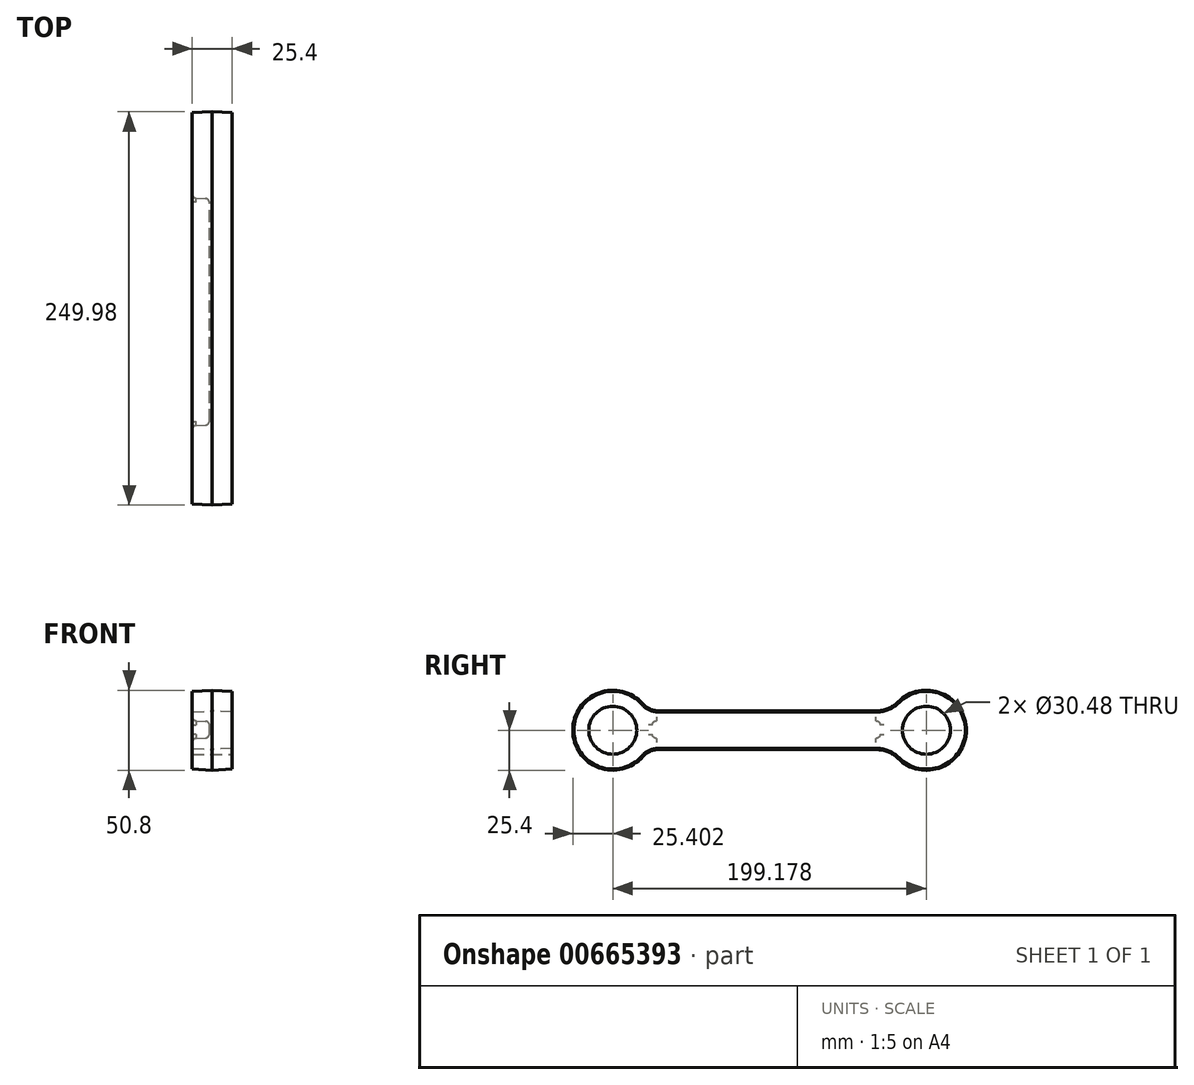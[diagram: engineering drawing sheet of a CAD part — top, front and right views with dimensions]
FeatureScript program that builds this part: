
annotation { "Feature Type Name" : "Feature", "Feature Type Description" : "" }
export const myFeature = defineFeature(function(context is Context, id is Id, definition is map)
    precondition{}
    {
        {
            var Q0;
            Q0=qCreatedBy(makeId("Right.planeOp"),FACE);
            var sketch = newSketch(context, id + "F0", { "sketchPlane" : qUnion([Q0])});
            skArc(sketch, "E0", {"start": v(-93.34, 16.65) * mm, "mid": v(-121.4, 23.8) * mm, "end": v(-137.92, 0) * mm});
            skArc(sketch, "E1", {"start": v(112.06, 0) * mm, "mid": v(96.34, 23.48) * mm, "end": v(68.64, 17.9) * mm});
            skLineSegment(sketch, "E2.bottom", {"start": v(-83.75, 12.28) * mm, "end": v(55.13, 12.28) * mm});
            skArc(sketch, "E3.filletArc", {"start": v(55.13, 12.28) * mm, "mid": v(62.45, 13.74) * mm, "end": v(68.64, 17.9) * mm});
            skPoint(sketch, "E4.visualSharp", {"position": v(-90.28, 12.28) * mm});
            skArc(sketch, "E4.filletArc", {"start": v(-93.34, 16.65) * mm, "mid": v(-89.02, 13.42) * mm, "end": v(-83.75, 12.28) * mm});
            skPoint(sketch, "E5.visualSharp", {"position": v(-91.27, -13.91) * mm});
            skArc(sketch, "E6.MirrorCS", {"start": v(-93.34, -16.65) * mm, "mid": v(-121.4, -23.8) * mm, "end": v(-137.92, 0) * mm});
            skArc(sketch, "E7.MirrorCS", {"start": v(-93.34, -16.65) * mm, "mid": v(-89.02, -13.42) * mm, "end": v(-83.75, -12.28) * mm});
            skLineSegment(sketch, "E8.MirrorCS", {"start": v(-83.75, -12.28) * mm, "end": v(55.13, -12.28) * mm});
            skArc(sketch, "E9.MirrorCS", {"start": v(55.13, -12.28) * mm, "mid": v(62.45, -13.74) * mm, "end": v(68.64, -17.9) * mm});
            skArc(sketch, "E10.MirrorCS", {"start": v(112.06, 0) * mm, "mid": v(96.34, -23.48) * mm, "end": v(68.64, -17.9) * mm});
            skLineSegment(sketch, "E11", {"start": v(-150.27, 0) * mm, "end": v(136.55, 0) * mm, "construction": true});
            skSolve(sketch);
        }
        {
            var Q0;
            Q0=makeQuery(id+"F0.imprint","IMPRINT",FACE,{"disambiguationData":[TD([[makeQuery(id+"F0.imprint","IMPRINT",EDGE,{"derivedFrom":sQuery(id+"F0.wireOp",EDGE,"E0")}),1.0]])]});
            extrude(context, id + "F1", {"entities" : qUnion([Q0]), "depth" : 12.7 * mm, "offsetDistance" : 25.4 * mm, "hasDraft" : true, "draftAngle" : 3 * degree, "draftPullDirection" : true, "hasSecondDirection" : true, "secondDirectionOppositeDirection" : true, "secondDirectionDepth" : 12.7 * mm, "hasSecondDirectionDraft" : true, "secondDirectionDraftAngle" : 3 * degree, "secondDirectionDraftPullDirection" : true});
        }
        {
            var Q0;
            Q0=qCreatedBy(makeId("Right.planeOp"),FACE);
            var sketch = newSketch(context, id + "F2", { "sketchPlane" : qUnion([Q0])});
            skCircle(sketch, "E12", {"center": v(-112.52, 0) * mm, "radius": 15.24 * mm});
            skCircle(sketch, "E13", {"center": v(86.66, 0) * mm, "radius": 15.24 * mm});
            skSolve(sketch);
        }
        {
            var Q0;
            Q0 = qSketchRegion(id + "F2", true);
            extrude(context, id + "F3", {"entities" : qUnion([Q0]), "operationType" : NewBodyOperationType.REMOVE, "oppositeDirection" : true, "depth" : 40.64 * mm, "offsetDistance" : 25.4 * mm, "hasSecondDirection" : true, "secondDirectionOppositeDirection" : false, "secondDirectionDepth" : 25.4 * mm});
        }
        {
            var Q0;
            Q0=qCreatedBy(makeId("Right.planeOp"),FACE);
            var sketch = newSketch(context, id + "F4", { "sketchPlane" : qUnion([Q0])});
            skLineSegment(sketch, "E14.bottom", {"start": v(-86.75, 5.5) * mm, "end": v(56.67, 5.5) * mm});
            skLineSegment(sketch, "E14.top", {"start": v(-86.75, -4.65) * mm, "end": v(56.67, -4.65) * mm});
            skLineSegment(sketch, "E14.left", {"start": v(-86.75, 5.5) * mm, "end": v(-86.75, -4.65) * mm});
            skLineSegment(sketch, "E14.right", {"start": v(56.67, 5.5) * mm, "end": v(56.67, -4.65) * mm});
            skSolve(sketch);
        }
        {
            var Q0;
            Q0 = qSketchRegion(id + "F4", true);
            extrude(context, id + "F5", {"entities" : qUnion([Q0]), "operationType" : NewBodyOperationType.REMOVE, "oppositeDirection" : true, "depth" : 25.4 * mm, "offsetDistance" : 25.4 * mm, "hasDraft" : true, "draftAngle" : 3 * degree, "hasSecondDirection" : true, "secondDirectionOppositeDirection" : true, "secondDirectionDepth" : 1.78 * mm});
        }
        {
            var Q0;
            Q0=makeQuery(id+"F5.boolean.opBoolean","COPY",FACE,{"derivedFrom":makeQuery(id+"F5.opExtrude","CAP_FACE",FACE,{"disambiguationData":[OSD([sQuery(id+"F4.wireOp",EDGE,"E14.bottom"),sQuery(id+"F4.wireOp",EDGE,"E14.top"),sQuery(id+"F4.wireOp",EDGE,"E14.left"),sQuery(id+"F4.wireOp",EDGE,"E14.right")])],"isStart":true})});
            var Q1;
            Q1=makeQuery(id+"F5.boolean.opBoolean","COPY",FACE,{"derivedFrom":makeQuery(id+"F5.opExtrude","SWEPT_FACE",FACE,{"disambiguationData":[OSD([sQuery(id+"F4.wireOp",EDGE,"E14.bottom")])]})});
            var Q2;
            Q2=makeQuery(id+"F5.boolean.opBoolean","COPY",FACE,{"derivedFrom":makeQuery(id+"F5.opExtrude","SWEPT_FACE",FACE,{"disambiguationData":[OSD([sQuery(id+"F4.wireOp",EDGE,"E14.right")])]})});
            var Q3;
            Q3=makeQuery(id+"F5.boolean.opBoolean","COPY",FACE,{"derivedFrom":makeQuery(id+"F5.opExtrude","SWEPT_FACE",FACE,{"disambiguationData":[OSD([sQuery(id+"F4.wireOp",EDGE,"E14.top")])]})});
            var Q4;
            Q4=makeQuery(id+"F5.boolean.opBoolean","COPY",FACE,{"derivedFrom":makeQuery(id+"F5.opExtrude","SWEPT_FACE",FACE,{"disambiguationData":[OSD([sQuery(id+"F4.wireOp",EDGE,"E14.left")])]})});
            var Q5;
            Q5=makeQuery(id+"FS2n0hhe4gk8Koj_1.1.F5.boolean.opBoolean","COPY",FACE,{"derivedFrom":makeQuery(id+"FS2n0hhe4gk8Koj_1.1.F5.opExtrude","SWEPT_FACE",FACE,{"disambiguationData":[OSD([sQuery(id+"F4.wireOp",EDGE,"E14.bottom")])]})});
            var Q6;
            Q6=makeQuery(id+"FS2n0hhe4gk8Koj_1.1.F5.boolean.opBoolean","COPY",FACE,{"derivedFrom":makeQuery(id+"FS2n0hhe4gk8Koj_1.1.F5.opExtrude","SWEPT_FACE",FACE,{"disambiguationData":[OSD([sQuery(id+"F4.wireOp",EDGE,"E14.left")])]})});
            var Q7;
            Q7=makeQuery(id+"FS2n0hhe4gk8Koj_1.1.F5.boolean.opBoolean","COPY",FACE,{"derivedFrom":makeQuery(id+"FS2n0hhe4gk8Koj_1.1.F5.opExtrude","SWEPT_FACE",FACE,{"disambiguationData":[OSD([sQuery(id+"F4.wireOp",EDGE,"E14.top")])]})});
            var Q8;
            Q8=makeQuery(id+"FS2n0hhe4gk8Koj_1.1.F5.boolean.opBoolean","COPY",FACE,{"derivedFrom":makeQuery(id+"FS2n0hhe4gk8Koj_1.1.F5.opExtrude","SWEPT_FACE",FACE,{"disambiguationData":[OSD([sQuery(id+"F4.wireOp",EDGE,"E14.right")])]})});
            fillet(context, id + "F6", {"entities" : qUnion([Q0, Q1, Q2, Q3, Q4, Q5, Q6, Q7, Q8]), "radius" : 2.54 * mm, "tangentPropagation" : true, "allowEdgeOverflow" : false});
        }
    });
